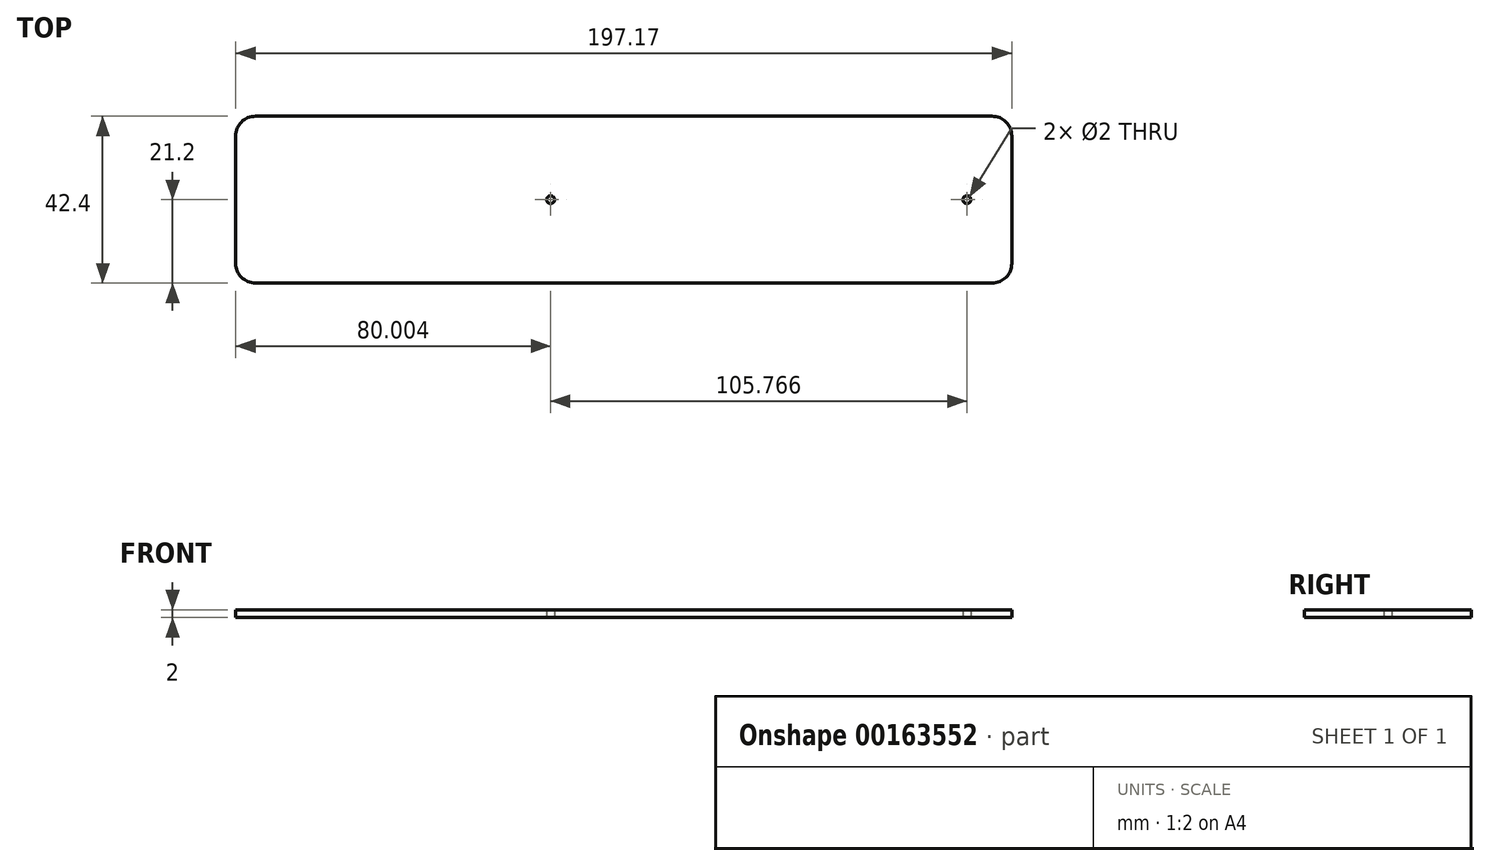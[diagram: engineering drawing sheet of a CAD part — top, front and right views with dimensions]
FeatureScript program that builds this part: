
annotation { "Feature Type Name" : "Feature", "Feature Type Description" : "" }
export const myFeature = defineFeature(function(context is Context, id is Id, definition is map)
    precondition{}
    {
        {
            var Q0;
            Q0=qCreatedBy(makeId("Top.planeOp"),FACE);
            var sketch = newSketch(context, id + "F0", { "sketchPlane" : qUnion([Q0])});
            skLineSegment(sketch, "E0.bottom", {"start": v(-165.17, 21.2) * mm, "end": v(32, 21.2) * mm});
            skLineSegment(sketch, "E0.top", {"start": v(-165.17, -21.2) * mm, "end": v(32, -21.2) * mm});
            skLineSegment(sketch, "E0.left", {"start": v(-165.17, 21.2) * mm, "end": v(-165.17, -21.2) * mm});
            skLineSegment(sketch, "E0.right", {"start": v(32, 21.2) * mm, "end": v(32, -21.2) * mm});
            skCircle(sketch, "E1", {"center": v(20.6, 0) * mm, "radius": 1 * mm});
            skCircle(sketch, "E2", {"center": v(-85.17, 0) * mm, "radius": 1 * mm});
            skSolve(sketch);
        }
        {
            var Q0;
            Q0=qSketchRegion(id+"F0",true);
            var Q1;
            Q1=makeQuery(id+"F0.imprint","IMPRINT",FACE,{"disambiguationData":[TD([[makeQuery(id+"F0.imprint","IMPRINT",EDGE,{"derivedFrom":sQuery(id+"F0.wireOp",EDGE,"E0.bottom")}),-1.0]])]});
            extrude(context, id + "F1", {"entities" : qUnion([Q0, Q1]), "depth" : 2 * mm});
        }
        {
            var Q0;
            Q0=makeQuery(id+"F1.opExtrude","SWEPT_EDGE",EDGE,{"disambiguationData":[OSD([sQuery(id+"F0.wireOp",EDGE,"E0.top"),sQuery(id+"F0.wireOp",EDGE,"E0.right")])]});
            var Q1;
            Q1=makeQuery(id+"F1.opExtrude","SWEPT_EDGE",EDGE,{"disambiguationData":[OSD([sQuery(id+"F0.wireOp",EDGE,"E0.bottom"),sQuery(id+"F0.wireOp",EDGE,"E0.right")])]});
            var Q2;
            Q2=makeQuery(id+"F1.opExtrude","SWEPT_EDGE",EDGE,{"disambiguationData":[OSD([sQuery(id+"F0.wireOp",EDGE,"E0.bottom"),sQuery(id+"F0.wireOp",EDGE,"E0.left")])]});
            var Q3;
            Q3=makeQuery(id+"F1.opExtrude","SWEPT_EDGE",EDGE,{"disambiguationData":[OSD([sQuery(id+"F0.wireOp",EDGE,"E0.top"),sQuery(id+"F0.wireOp",EDGE,"E0.left")])]});
            fillet(context, id + "F2", {"entities" : qUnion([Q0, Q1, Q2, Q3]), "radius" : 5 * mm, "tangentPropagation" : true, "allowEdgeOverflow" : false});
        }
    });
